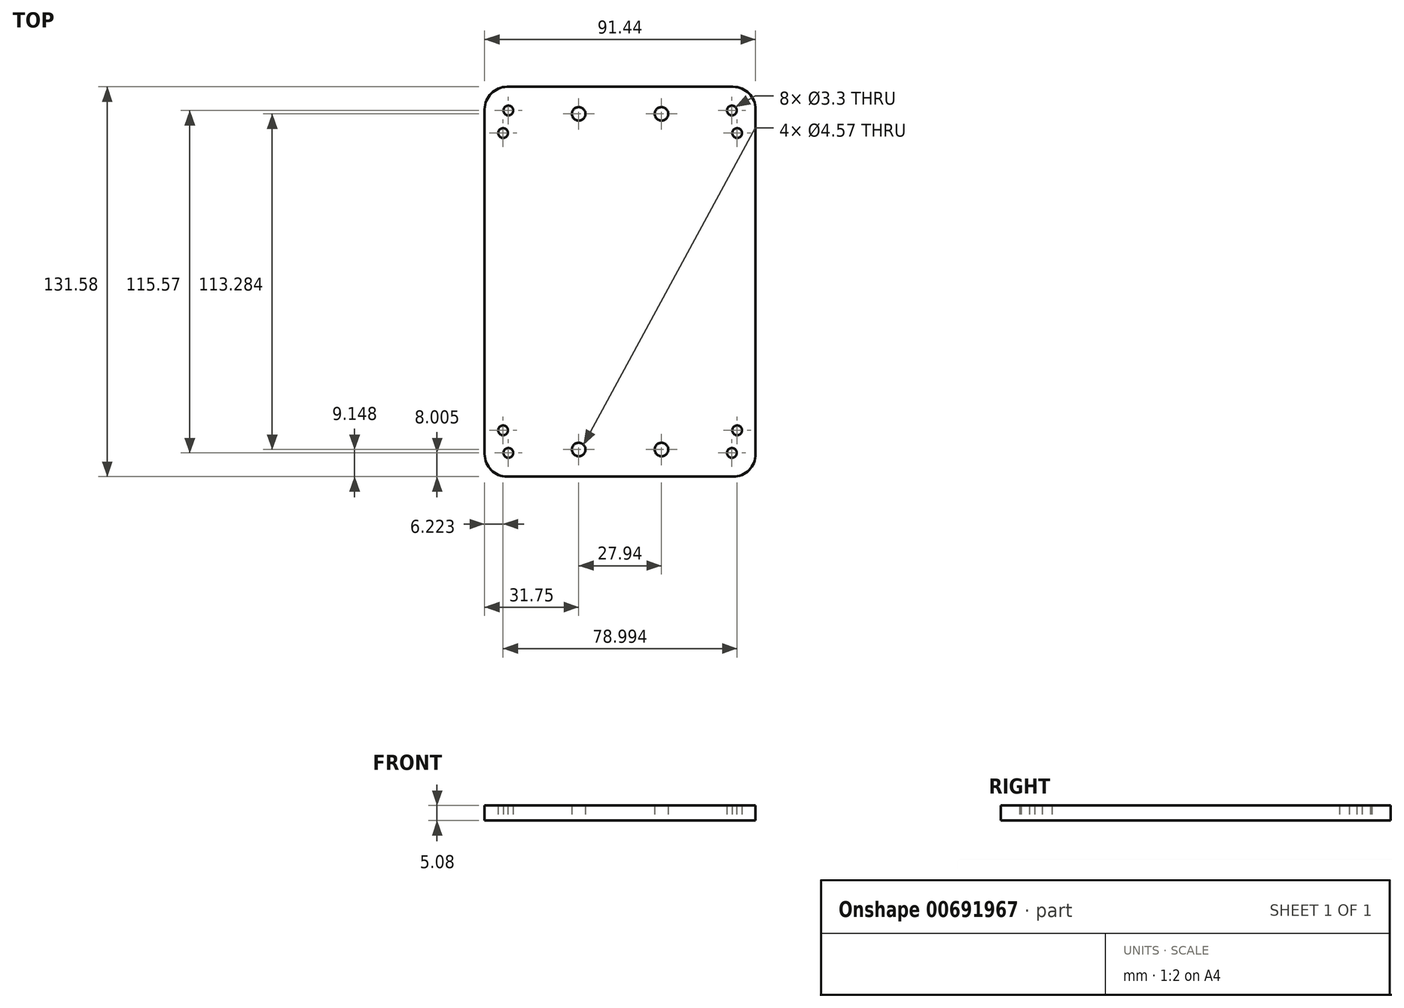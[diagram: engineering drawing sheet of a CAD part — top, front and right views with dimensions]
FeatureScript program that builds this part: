
annotation { "Feature Type Name" : "Feature", "Feature Type Description" : "" }
export const myFeature = defineFeature(function(context is Context, id is Id, definition is map)
    precondition{}
    {
        {
            var Q0;
            Q0=qCreatedBy(makeId("Top.planeOp"),FACE);
            var sketch = newSketch(context, id + "F0", { "sketchPlane" : qUnion([Q0])});
            skLineSegment(sketch, "E0.bottom", {"start": v(-45.72, 65.79) * mm, "end": v(45.72, 65.79) * mm});
            skLineSegment(sketch, "E0.top", {"start": v(-45.72, -65.79) * mm, "end": v(45.72, -65.79) * mm});
            skLineSegment(sketch, "E0.left", {"start": v(-45.72, 65.79) * mm, "end": v(-45.72, -65.79) * mm});
            skLineSegment(sketch, "E0.right", {"start": v(45.72, 65.79) * mm, "end": v(45.72, -65.79) * mm});
            skPoint(sketch, "E0.middle", {"position": v(0, 0) * mm});
            skCircle(sketch, "E1", {"center": v(13.97, -56.64) * mm, "radius": 2.29 * mm});
            skCircle(sketch, "E2", {"center": v(37.72, -57.78) * mm, "radius": 1.65 * mm});
            skCircle(sketch, "E3", {"center": v(39.5, -50.16) * mm, "radius": 1.65 * mm});
            skCircle(sketch, "E4.MirrorC", {"center": v(-13.97, -56.64) * mm, "radius": 2.29 * mm});
            skCircle(sketch, "E5.MirrorC", {"center": v(-37.72, -57.78) * mm, "radius": 1.65 * mm});
            skCircle(sketch, "E6.MirrorC", {"center": v(-39.5, -50.16) * mm, "radius": 1.65 * mm});
            skCircle(sketch, "E7.MirrorC", {"center": v(39.5, 50.16) * mm, "radius": 1.65 * mm});
            skCircle(sketch, "E8.MirrorC", {"center": v(37.72, 57.78) * mm, "radius": 1.65 * mm});
            skCircle(sketch, "E9.MirrorC", {"center": v(13.97, 56.64) * mm, "radius": 2.29 * mm});
            skCircle(sketch, "E10.MirrorC", {"center": v(-13.97, 56.64) * mm, "radius": 2.29 * mm});
            skCircle(sketch, "E11.MirrorC", {"center": v(-37.72, 57.78) * mm, "radius": 1.65 * mm});
            skCircle(sketch, "E12.MirrorC", {"center": v(-39.5, 50.16) * mm, "radius": 1.65 * mm});
            skSolve(sketch);
        }
        {
            var Q0;
            Q0=makeQuery(id+"F0.imprint","IMPRINT",FACE,{"disambiguationData":[TD([[makeQuery(id+"F0.imprint","IMPRINT",EDGE,{"derivedFrom":sQuery(id+"F0.wireOp",EDGE,"E0.bottom")}),-1.0]])]});
            extrude(context, id + "F1", {"entities" : qUnion([Q0]), "depth" : 5.08 * mm, "offsetDistance" : 25.4 * mm});
        }
        {
            var Q0;
            Q0=makeQuery(id+"F1.opExtrude","SWEPT_EDGE",EDGE,{"disambiguationData":[OSD([sQuery(id+"F0.wireOp",EDGE,"E0.bottom"),sQuery(id+"F0.wireOp",EDGE,"E0.left")])]});
            var Q1;
            Q1=makeQuery(id+"F1.opExtrude","SWEPT_EDGE",EDGE,{"disambiguationData":[OSD([sQuery(id+"F0.wireOp",EDGE,"E0.bottom"),sQuery(id+"F0.wireOp",EDGE,"E0.right")])]});
            var Q2;
            Q2=makeQuery(id+"F1.opExtrude","SWEPT_EDGE",EDGE,{"disambiguationData":[OSD([sQuery(id+"F0.wireOp",EDGE,"E0.top"),sQuery(id+"F0.wireOp",EDGE,"E0.right")])]});
            var Q3;
            Q3=makeQuery(id+"F1.opExtrude","SWEPT_EDGE",EDGE,{"disambiguationData":[OSD([sQuery(id+"F0.wireOp",EDGE,"E0.top"),sQuery(id+"F0.wireOp",EDGE,"E0.left")])]});
            fillet(context, id + "F2", {"entities" : qUnion([Q0, Q1, Q2, Q3]), "radius" : 7.62 * mm, "tangentPropagation" : true, "allowEdgeOverflow" : false});
        }
    });
